# Revit family: Diverter_Trim-GROHE-Concetto_3-29106001
name_source: partatom
category: Plumbing Fixtures
revit_build: Autodesk Revit 2014 (Build: 20130308_1515(x64)
units: mm (PartAtom-declared; Revit-internal decimal feet)

## types (1)
- 29106001
    ADA Compliant = Yes
    Assembly Code = D2020
    CW Connection = Yes
    CWFU = 2
    Default Elevation = 0"
    Description = Concetto 3-Way Diverter Trim (Shower head/Hand Shower/Tub Spout)
    Finish = Metal-Grohe-000-Chrome
    HW Connection = Yes
    HWFU = 3
    Height = 4 13/16"
    IAPMO Compliance = cUPC
    Installation Type = Surface Mounted
    Length = 2 5/8"
    Manufacturer = GROHE
    Material = Ceramic-Grohe-000-Starlight Chrome
    Model = 29106001
    Price = Prices may vary. Please consult Manufacturer Representative for most up-to-date price list.
    Product Page URL = https://www.grohe.ca
    Tempered Water Connection Diameter = 1/2"
    Tempered Water Connection Radius = 1/4"
    URL = http://www.grohe.com
    Vent Connection = No
    WFU = 4
    Warranty Information = Limited Lifetime Warranty
    Waste Connection = No
    Width = 3 1/8"

## geometry (parser evidence)
native form markers: Sweep x3
no freeform markers — native parametric forms only
